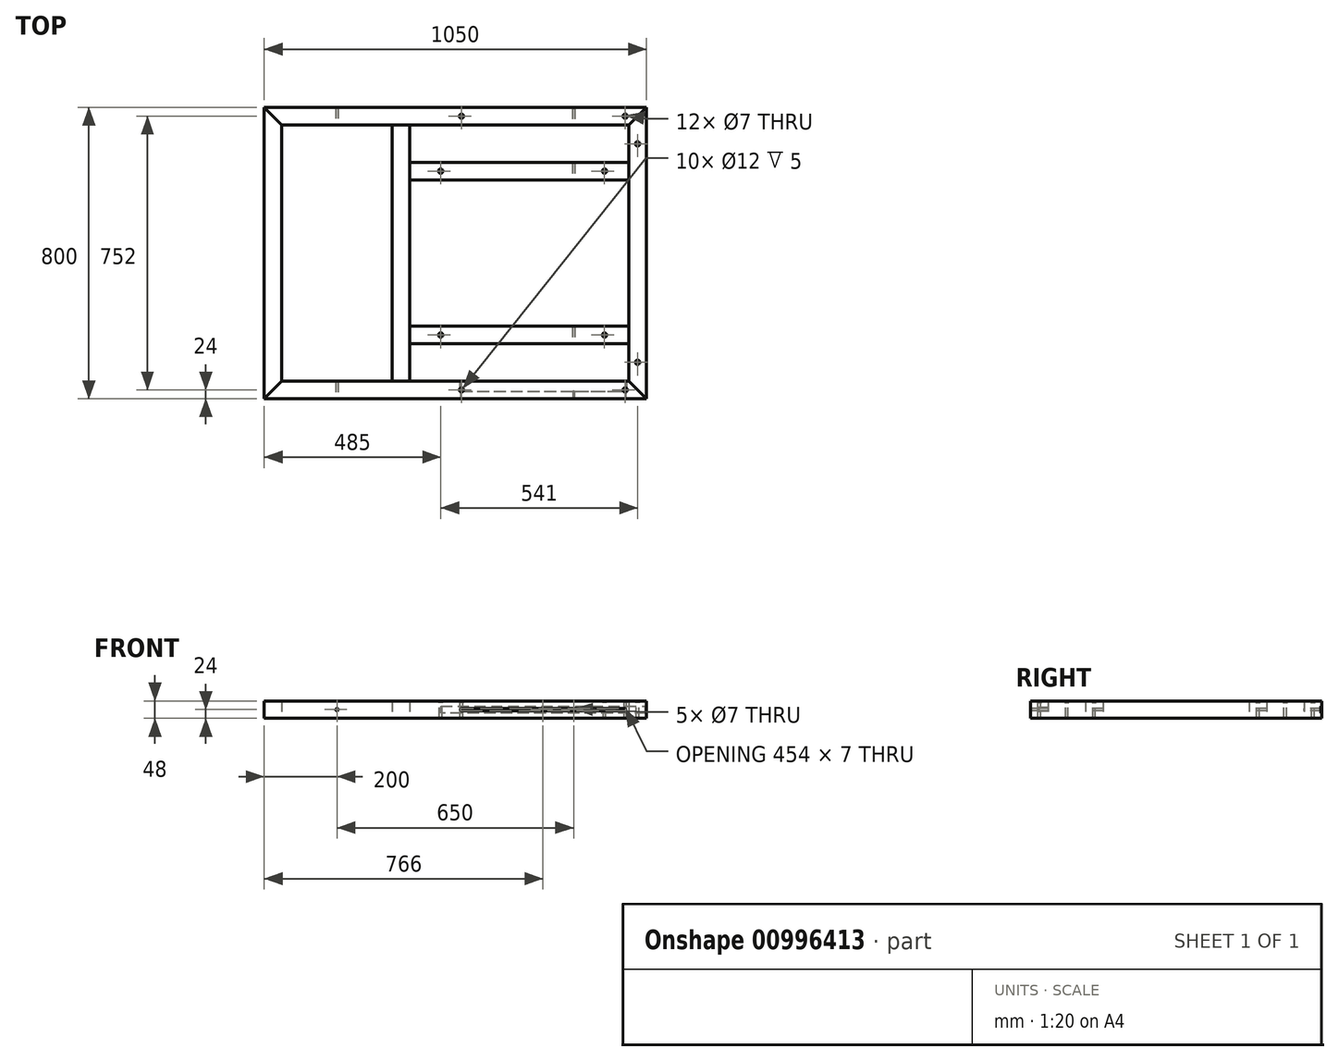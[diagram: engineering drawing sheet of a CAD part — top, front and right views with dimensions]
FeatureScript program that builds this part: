
annotation { "Feature Type Name" : "Feature", "Feature Type Description" : "" }
export const myFeature = defineFeature(function(context is Context, id is Id, definition is map)
    precondition{}
    {
        {
            var Q0;
            Q0=qCreatedBy(makeId("Top.planeOp"),FACE);
            var sketch = newSketch(context, id + "F0", { "sketchPlane" : qUnion([Q0])});
            skLineSegment(sketch, "E0", {"start": v(0, 0) * mm, "end": v(1050, 0) * mm});
            skLineSegment(sketch, "E1", {"start": v(1050, 0) * mm, "end": v(1050, 800) * mm});
            skLineSegment(sketch, "E2", {"start": v(1050, 800) * mm, "end": v(0, 800) * mm});
            skLineSegment(sketch, "E3", {"start": v(0, 800) * mm, "end": v(0, 0) * mm});
            skLineSegment(sketch, "E4", {"start": v(48, 752) * mm, "end": v(48, 48) * mm});
            skLineSegment(sketch, "E5", {"start": v(48, 48) * mm, "end": v(1002, 48) * mm});
            skLineSegment(sketch, "E6", {"start": v(1002, 48) * mm, "end": v(1002, 752) * mm});
            skLineSegment(sketch, "E7", {"start": v(1002, 752) * mm, "end": v(48, 752) * mm});
            skLineSegment(sketch, "E8", {"start": v(0, 800) * mm, "end": v(48, 752) * mm});
            skLineSegment(sketch, "E9", {"start": v(1002, 752) * mm, "end": v(1050, 800) * mm});
            skLineSegment(sketch, "E10", {"start": v(1002, 48) * mm, "end": v(1050, 0) * mm});
            skLineSegment(sketch, "E11", {"start": v(0, 0) * mm, "end": v(48, 48) * mm});
            skPoint(sketch, "E12.end.orphan", {"position": v(1002, 400) * mm});
            skLineSegment(sketch, "E13", {"start": v(352, 752) * mm, "end": v(352, 48) * mm});
            skLineSegment(sketch, "E14", {"start": v(352, 48) * mm, "end": v(400, 48) * mm});
            skLineSegment(sketch, "E15", {"start": v(400, 48) * mm, "end": v(400, 752) * mm});
            skLineSegment(sketch, "E16", {"start": v(400, 601) * mm, "end": v(1002, 601) * mm});
            skLineSegment(sketch, "E17", {"start": v(400, 199) * mm, "end": v(1002, 199) * mm});
            skLineSegment(sketch, "E18", {"start": v(400, 151) * mm, "end": v(1002, 151) * mm});
            skLineSegment(sketch, "E19", {"start": v(400, 649) * mm, "end": v(1002, 649) * mm});
            skSolve(sketch);
        }
        {
            var Q0;
            Q0=makeQuery(id+"F0.imprint","IMPRINT",FACE,{"disambiguationData":[TD([[makeQuery(id+"F0.imprint","IMPRINT",EDGE,{"derivedFrom":sQuery(id+"F0.wireOp",EDGE,"E3")}),1.0]])]});
            extrude(context, id + "F1", {"entities" : qUnion([Q0]), "depth" : 48 * mm, "offsetDistance" : 25 * mm});
        }
        {
            var Q0;
            Q0=makeQuery(id+"F0.imprint","IMPRINT",FACE,{"disambiguationData":[TD([[makeQuery(id+"F0.imprint","IMPRINT",EDGE,{"derivedFrom":sQuery(id+"F0.wireOp",EDGE,"E0")}),1.0]])]});
            extrude(context, id + "F2", {"entities" : qUnion([Q0]), "depth" : 48 * mm, "offsetDistance" : 25 * mm});
        }
        {
            var Q0;
            Q0=makeQuery(id+"F0.imprint","IMPRINT",FACE,{"disambiguationData":[TD([[makeQuery(id+"F0.imprint","IMPRINT",EDGE,{"derivedFrom":sQuery(id+"F0.wireOp",EDGE,"E1")}),1.0]])]});
            extrude(context, id + "F3", {"entities" : qUnion([Q0]), "depth" : 48 * mm, "offsetDistance" : 25 * mm});
        }
        {
            var Q0;
            Q0=makeQuery(id+"F0.imprint","IMPRINT",FACE,{"disambiguationData":[TD([[makeQuery(id+"F0.imprint","IMPRINT",EDGE,{"derivedFrom":sQuery(id+"F0.wireOp",EDGE,"E2")}),1.0]])]});
            extrude(context, id + "F4", {"entities" : qUnion([Q0]), "depth" : 48 * mm, "offsetDistance" : 25 * mm});
        }
        {
            var Q0;
            {var subQ3=sQuery(id+"F0.wireOp",EDGE,"E13");Q0=makeQuery(id+"F0.imprint","IMPRINT",FACE,{"disambiguationData":[TD([[makeQuery(id+"F0.imprint","IMPRINT",EDGE,{"derivedFrom":subQ3}),1.0]])]});}
            extrude(context, id + "F5", {"entities" : qUnion([Q0]), "depth" : 48 * mm, "offsetDistance" : 25 * mm});
        }
        {
            var Q0;
            {var subQ0=sQuery(id+"F0.wireOp",EDGE,"E17");Q0=makeQuery(id+"F0.imprint","IMPRINT",FACE,{"disambiguationData":[TD([[makeQuery(id+"F0.imprint","IMPRINT",EDGE,{"derivedFrom":subQ0}),-1.0]])]});}
            extrude(context, id + "F6", {"entities" : qUnion([Q0]), "depth" : 48 * mm, "offsetDistance" : 25 * mm});
        }
        {
            var Q0;
            {var subQ0=sQuery(id+"F0.wireOp",EDGE,"E16");Q0=makeQuery(id+"F0.imprint","IMPRINT",FACE,{"disambiguationData":[TD([[makeQuery(id+"F0.imprint","IMPRINT",EDGE,{"derivedFrom":subQ0}),1.0]])]});}
            extrude(context, id + "F7", {"entities" : qUnion([Q0]), "depth" : 48 * mm, "offsetDistance" : 25 * mm});
        }
        {
            var Q0;
            Q0=makeQuery(id+"F4.opExtrude","CAP_FACE",FACE,{"disambiguationData":[OSD([sQuery(id+"F0.wireOp",EDGE,"E2"),sQuery(id+"F0.wireOp",EDGE,"E7"),sQuery(id+"F0.wireOp",EDGE,"E8"),sQuery(id+"F0.wireOp",EDGE,"E9")])],"isStart":false});
            var sketch = newSketch(context, id + "F8", { "sketchPlane" : qUnion([Q0])});
            skLineSegment(sketch, "E20", {"start": v(1026, 700) * mm, "end": v(1026, 706) * mm});
            skPoint(sketch, "E20.startSnap0", {"position": v(1026, 776) * mm});
            skCircle(sketch, "E21", {"center": v(1026, 700) * mm, "radius": 6 * mm});
            skCircle(sketch, "E22.0.1.0", {"center": v(1026, 100) * mm, "radius": 6 * mm});
            skLineSegment(sketch, "E22.direction1", {"start": v(1026, 700) * mm, "end": v(1051, 700) * mm, "construction": true});
            skLineSegment(sketch, "E22.direction2", {"start": v(1026, 700) * mm, "end": v(1026, 100) * mm, "construction": true});
            skCircle(sketch, "E23", {"center": v(992, 776) * mm, "radius": 6 * mm});
            skCircle(sketch, "E24.0.1.0", {"center": v(992, 24) * mm, "radius": 6 * mm});
            skCircle(sketch, "E24.1.0.0", {"center": v(542, 776) * mm, "radius": 6 * mm});
            skCircle(sketch, "E24.1.1.0", {"center": v(542, 24) * mm, "radius": 6 * mm});
            skLineSegment(sketch, "E24.direction1", {"start": v(992, 776) * mm, "end": v(542, 776) * mm, "construction": true});
            skLineSegment(sketch, "E24.direction2", {"start": v(992, 776) * mm, "end": v(992, 24) * mm, "construction": true});
            skCircle(sketch, "E25", {"center": v(935, 625) * mm, "radius": 6 * mm});
            skCircle(sketch, "E26.0.1.0", {"center": v(935, 175) * mm, "radius": 6 * mm});
            skCircle(sketch, "E26.1.0.0", {"center": v(485, 625) * mm, "radius": 6 * mm});
            skCircle(sketch, "E26.1.1.0", {"center": v(485, 175) * mm, "radius": 6 * mm});
            skLineSegment(sketch, "E26.direction1", {"start": v(935, 625) * mm, "end": v(485, 625) * mm, "construction": true});
            skLineSegment(sketch, "E26.direction2", {"start": v(935, 625) * mm, "end": v(935, 175) * mm, "construction": true});
            skSolve(sketch);
        }
        {
            var Q0;
            Q0=makeQuery(id+"F8.imprint","IMPRINT",FACE,{"disambiguationData":[TD([[makeQuery(id+"F8.imprint","IMPRINT",EDGE,{"derivedFrom":sQuery(id+"F8.wireOp",EDGE,"E23")}),-1.0]])]});
            var sketch = newSketch(context, id + "F9", { "sketchPlane" : qUnion([Q0])});
            skLineSegment(sketch, "E27", {"start": v(1026, 700) * mm, "end": v(1026, 703.5) * mm});
            skPoint(sketch, "E27.startSnap0", {"position": v(1026, 776) * mm});
            skCircle(sketch, "E28", {"center": v(1026, 700) * mm, "radius": 3.5 * mm});
            skCircle(sketch, "E29.0.1.0", {"center": v(1026, 100) * mm, "radius": 3.5 * mm});
            skLineSegment(sketch, "E29.direction1", {"start": v(1026, 700) * mm, "end": v(1051, 700) * mm, "construction": true});
            skLineSegment(sketch, "E29.direction2", {"start": v(1026, 700) * mm, "end": v(1026, 100) * mm, "construction": true});
            skCircle(sketch, "E30", {"center": v(992, 776) * mm, "radius": 3.5 * mm});
            skCircle(sketch, "E31.0.1.0", {"center": v(992, 24) * mm, "radius": 3.5 * mm});
            skCircle(sketch, "E31.1.0.0", {"center": v(542, 776) * mm, "radius": 3.5 * mm});
            skCircle(sketch, "E31.1.1.0", {"center": v(542, 24) * mm, "radius": 3.5 * mm});
            skLineSegment(sketch, "E31.direction1", {"start": v(992, 776) * mm, "end": v(542, 776) * mm, "construction": true});
            skLineSegment(sketch, "E31.direction2", {"start": v(992, 776) * mm, "end": v(992, 24) * mm, "construction": true});
            skCircle(sketch, "E32", {"center": v(935, 625) * mm, "radius": 3.5 * mm});
            skCircle(sketch, "E33.0.1.0", {"center": v(935, 175) * mm, "radius": 3.5 * mm});
            skCircle(sketch, "E33.1.0.0", {"center": v(485, 625) * mm, "radius": 3.5 * mm});
            skCircle(sketch, "E33.1.1.0", {"center": v(485, 175) * mm, "radius": 3.5 * mm});
            skLineSegment(sketch, "E33.direction1", {"start": v(935, 625) * mm, "end": v(485, 625) * mm, "construction": true});
            skLineSegment(sketch, "E33.direction2", {"start": v(935, 625) * mm, "end": v(935, 175) * mm, "construction": true});
            skSolve(sketch);
        }
        {
            var Q0;
            Q0 = qSketchRegion(id + "F8", true);
            extrude(context, id + "F10", {"entities" : qUnion([Q0]), "operationType" : NewBodyOperationType.REMOVE, "oppositeDirection" : true, "depth" : 5 * mm, "offsetDistance" : 25 * mm});
        }
        {
            var Q0;
            Q0 = qSketchRegion(id + "F9", true);
            extrude(context, id + "F11", {"entities" : qUnion([Q0]), "operationType" : NewBodyOperationType.REMOVE, "endBound" : BoundingType.THROUGH_ALL, "oppositeDirection" : true, "depth" : 25 * mm, "offsetDistance" : 25 * mm});
        }
        {
            var Q0;
            Q0=makeQuery(id+"F2.opExtrude","SWEPT_FACE",FACE,{"disambiguationData":[OSD([sQuery(id+"F0.wireOp",EDGE,"E0")])]});
            var sketch = newSketch(context, id + "F12", { "sketchPlane" : qUnion([Q0])});
            skLineSegment(sketch, "E34", {"start": v(0, 24) * mm, "end": v(200, 24) * mm});
            skLineSegment(sketch, "E35", {"start": v(200, 24) * mm, "end": v(200, 48) * mm});
            skLineSegment(sketch, "E36", {"start": v(200, 24) * mm, "end": v(200, 0) * mm});
            skCircle(sketch, "E37", {"center": v(200, 24) * mm, "radius": 3.5 * mm});
            skLineSegment(sketch, "E38", {"start": v(1050, 24) * mm, "end": v(850, 24) * mm});
            skLineSegment(sketch, "E39", {"start": v(850, 24) * mm, "end": v(850, 48) * mm});
            skLineSegment(sketch, "E40", {"start": v(850, 24) * mm, "end": v(850, 0) * mm});
            skCircle(sketch, "E41", {"center": v(850, 24) * mm, "radius": 3.5 * mm});
            skSolve(sketch);
        }
        {
            var Q0;
            {var subQ1=sQuery(id+"F12.wireOp",EDGE,"E35");var subQ3=sQuery(id+"F12.wireOp",EDGE,"E37");var subQ4=makeQuery(id+"F12.imprint","INTERSECT",VERTEX,{"derivedFrom":[subQ1,subQ3]});Q0=makeQuery(id+"F12.imprint","IMPRINT",FACE,{"disambiguationData":[TD([[makeQuery(id+"F12.imprint","IMPRINT",EDGE,{"disambiguationData":[TD([[subQ4,1.0]])],"derivedFrom":subQ3}),1.0]])]});}
            var Q1;
            {var subQ1=sQuery(id+"F12.wireOp",EDGE,"E34");var subQ3=sQuery(id+"F12.wireOp",EDGE,"E37");var subQ4=makeQuery(id+"F12.imprint","INTERSECT",VERTEX,{"derivedFrom":[subQ1,subQ3]});Q1=makeQuery(id+"F12.imprint","IMPRINT",FACE,{"disambiguationData":[TD([[makeQuery(id+"F12.imprint","IMPRINT",EDGE,{"disambiguationData":[TD([[subQ4,-1.0]])],"derivedFrom":subQ3}),1.0]])]});}
            var Q2;
            {var subQ1=sQuery(id+"F12.wireOp",EDGE,"E34");var subQ3=sQuery(id+"F12.wireOp",EDGE,"E37");var subQ4=makeQuery(id+"F12.imprint","INTERSECT",VERTEX,{"derivedFrom":[subQ1,subQ3]});Q2=makeQuery(id+"F12.imprint","IMPRINT",FACE,{"disambiguationData":[TD([[makeQuery(id+"F12.imprint","IMPRINT",EDGE,{"disambiguationData":[TD([[subQ4,1.0]])],"derivedFrom":subQ3}),1.0]])]});}
            extrude(context, id + "F13", {"entities" : qUnion([Q0, Q1, Q2]), "operationType" : NewBodyOperationType.REMOVE, "endBound" : BoundingType.THROUGH_ALL, "oppositeDirection" : true, "depth" : 25 * mm, "offsetDistance" : 25 * mm});
        }
        {
            var Q0;
            {var subQ1=sQuery(id+"F12.wireOp",EDGE,"E39");var subQ3=sQuery(id+"F12.wireOp",EDGE,"E41");var subQ4=makeQuery(id+"F12.imprint","INTERSECT",VERTEX,{"derivedFrom":[subQ1,subQ3]});Q0=makeQuery(id+"F12.imprint","IMPRINT",FACE,{"disambiguationData":[TD([[makeQuery(id+"F12.imprint","IMPRINT",EDGE,{"disambiguationData":[TD([[subQ4,-1.0]])],"derivedFrom":subQ3}),1.0]])]});}
            var Q1;
            {var subQ1=sQuery(id+"F12.wireOp",EDGE,"E38");var subQ3=sQuery(id+"F12.wireOp",EDGE,"E41");var subQ4=makeQuery(id+"F12.imprint","INTERSECT",VERTEX,{"derivedFrom":[subQ1,subQ3]});Q1=makeQuery(id+"F12.imprint","IMPRINT",FACE,{"disambiguationData":[TD([[makeQuery(id+"F12.imprint","IMPRINT",EDGE,{"disambiguationData":[TD([[subQ4,1.0]])],"derivedFrom":subQ3}),1.0]])]});}
            var Q2;
            {var subQ1=sQuery(id+"F12.wireOp",EDGE,"E38");var subQ3=sQuery(id+"F12.wireOp",EDGE,"E41");var subQ4=makeQuery(id+"F12.imprint","INTERSECT",VERTEX,{"derivedFrom":[subQ1,subQ3]});Q2=makeQuery(id+"F12.imprint","IMPRINT",FACE,{"disambiguationData":[TD([[makeQuery(id+"F12.imprint","IMPRINT",EDGE,{"disambiguationData":[TD([[subQ4,-1.0]])],"derivedFrom":subQ3}),1.0]])]});}
            extrude(context, id + "F14", {"entities" : qUnion([Q0, Q1, Q2]), "operationType" : NewBodyOperationType.REMOVE, "endBound" : BoundingType.THROUGH_ALL, "oppositeDirection" : true, "depth" : 25 * mm, "offsetDistance" : 25 * mm});
        }
        {
            var Q0;
            Q0=qCreatedBy(makeId("Front.planeOp"),FACE);
            var sketch = newSketch(context, id + "F15", { "sketchPlane" : qUnion([Q0])});
            skLineSegment(sketch, "E42", {"start": v(0, 0) * mm, "end": v(0, 24) * mm});
            skLineSegment(sketch, "E43", {"start": v(0, 24) * mm, "end": v(0, 48) * mm});
            skLineSegment(sketch, "E44", {"start": v(0, 0) * mm, "end": v(1050, 0) * mm});
            skLineSegment(sketch, "E45", {"start": v(1050, 0) * mm, "end": v(1050, 24) * mm});
            skLineSegment(sketch, "E46", {"start": v(1050, 24) * mm, "end": v(1050, 48) * mm});
            skArc(sketch, "E47", {"start": v(542, 27) * mm, "mid": v(539, 24) * mm, "end": v(542, 21) * mm});
            skArc(sketch, "E48", {"start": v(990, 21) * mm, "mid": v(993, 24) * mm, "end": v(990, 27) * mm});
            skLineSegment(sketch, "E49", {"start": v(542, 27) * mm, "end": v(990, 27) * mm});
            skLineSegment(sketch, "E50", {"start": v(990, 21) * mm, "end": v(542, 21) * mm});
            skArc(sketch, "E51", {"start": v(992.55, 18.9) * mm, "mid": v(995.7, 24) * mm, "end": v(992.55, 29.1) * mm});
            skLineSegment(sketch, "E52", {"start": v(539.45, 18.9) * mm, "end": v(992.55, 18.9) * mm});
            skLineSegment(sketch, "E53", {"start": v(992.55, 29.1) * mm, "end": v(539.45, 29.1) * mm});
            skPoint(sketch, "E54.start.orphan", {"position": v(1122.55, 24) * mm});
            skArc(sketch, "E55.trimOffspring", {"start": v(539.45, 29.1) * mm, "mid": v(536.3, 24) * mm, "end": v(539.45, 18.9) * mm});
            skLineSegment(sketch, "E56", {"start": v(497, 34) * mm, "end": v(1050, 34) * mm});
            skLineSegment(sketch, "E57", {"start": v(1050, 34) * mm, "end": v(1050, 14) * mm});
            skLineSegment(sketch, "E58", {"start": v(1050, 14) * mm, "end": v(486, 14) * mm});
            skLineSegment(sketch, "E59", {"start": v(486, 14) * mm, "end": v(486, 34) * mm});
            skLineSegment(sketch, "E60", {"start": v(486, 34) * mm, "end": v(497, 34) * mm});
            skSolve(sketch);
        }
        {
            var Q0;
            Q0=makeQuery(id+"F15.imprint","IMPRINT",FACE,{"disambiguationData":[TD([[makeQuery(id+"F15.imprint","IMPRINT",EDGE,{"derivedFrom":sQuery(id+"F15.wireOp",EDGE,"E47")}),1.0]])]});
            extrude(context, id + "F16", {"entities" : qUnion([Q0]), "operationType" : NewBodyOperationType.REMOVE, "oppositeDirection" : true, "depth" : 50 * mm, "offsetDistance" : 25 * mm, "hasSecondDirection" : true, "secondDirectionOppositeDirection" : true, "secondDirectionDepth" : 0 * mm});
        }
        {
            var Q0;
            Q0=makeQuery(id+"F15.imprint","IMPRINT",FACE,{"disambiguationData":[TD([[makeQuery(id+"F15.imprint","IMPRINT",EDGE,{"derivedFrom":sQuery(id+"F15.wireOp",EDGE,"E47")}),-1.0]])]});
            extrude(context, id + "F17", {"entities" : qUnion([Q0]), "operationType" : NewBodyOperationType.REMOVE, "oppositeDirection" : true, "depth" : 50 * mm, "offsetDistance" : 25 * mm, "hasSecondDirection" : true, "secondDirectionOppositeDirection" : true, "secondDirectionDepth" : 20 * mm});
        }
        {
            var Q0;
            Q0 = qSketchRegion(id + "F15", true);
            var Q1;
            Q1=makeQuery(id+"F15.imprint","IMPRINT",FACE,{"disambiguationData":[TD([[makeQuery(id+"F15.imprint","IMPRINT",EDGE,{"derivedFrom":sQuery(id+"F15.wireOp",EDGE,"E47")}),-1.0]])]});
            var Q2;
            Q2=makeQuery(id+"F15.imprint","IMPRINT",FACE,{"disambiguationData":[TD([[makeQuery(id+"F15.imprint","IMPRINT",EDGE,{"derivedFrom":sQuery(id+"F15.wireOp",EDGE,"E47")}),1.0]])]});
            extrude(context, id + "F18", {"entities" : qUnion([Q0, Q1, Q2]), "operationType" : NewBodyOperationType.REMOVE, "oppositeDirection" : true, "depth" : 800 * mm, "offsetDistance" : 25 * mm, "hasSecondDirection" : true, "secondDirectionOppositeDirection" : true, "secondDirectionDepth" : 798 * mm});
        }
    });
